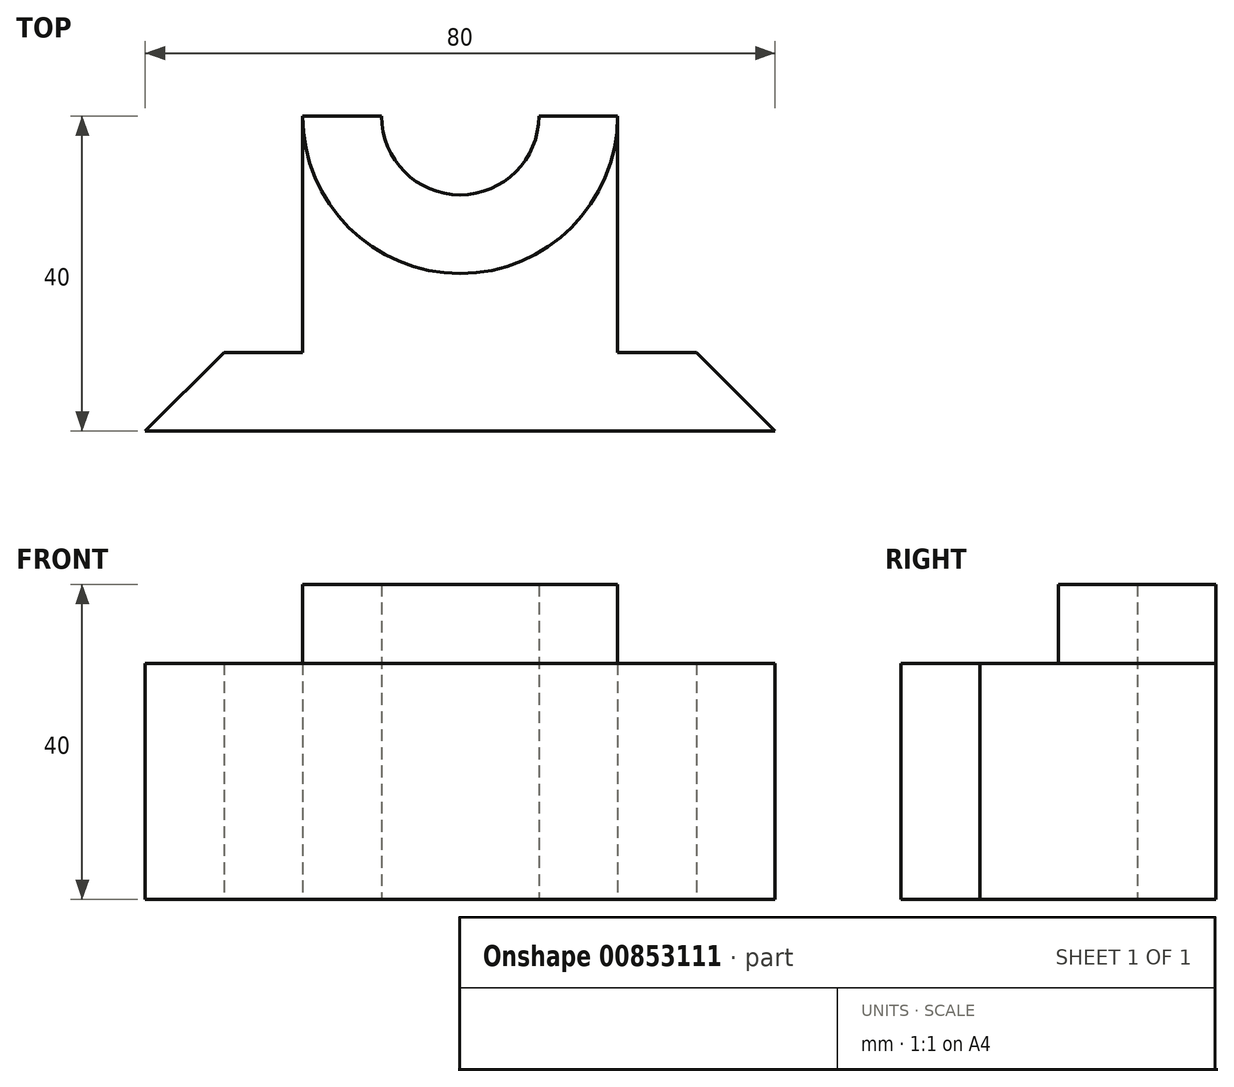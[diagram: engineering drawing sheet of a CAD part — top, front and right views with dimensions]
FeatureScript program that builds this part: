
annotation { "Feature Type Name" : "Feature", "Feature Type Description" : "" }
export const myFeature = defineFeature(function(context is Context, id is Id, definition is map)
    precondition{}
    {
        {
            var Q0;
            Q0=qCreatedBy(makeId("Top.planeOp"),FACE);
            var sketch = newSketch(context, id + "F0", { "sketchPlane" : qUnion([Q0])});
            skLineSegment(sketch, "E0", {"start": v(0, 30) * mm, "end": v(0, 0) * mm});
            skLineSegment(sketch, "E1", {"start": v(0, 0) * mm, "end": v(-40, 0) * mm});
            skLineSegment(sketch, "E2", {"start": v(-40, 0) * mm, "end": v(-30, 10) * mm});
            skLineSegment(sketch, "E3", {"start": v(-30, 10) * mm, "end": v(-20, 10) * mm});
            skLineSegment(sketch, "E4", {"start": v(-20, 10) * mm, "end": v(-20, 40) * mm});
            skLineSegment(sketch, "E5", {"start": v(-20, 40) * mm, "end": v(-10, 40) * mm});
            skArc(sketch, "E6", {"start": v(-20, 40) * mm, "mid": v(-14.14, 25.86) * mm, "end": v(0, 20) * mm});
            skArc(sketch, "E7", {"start": v(-10, 40) * mm, "mid": v(-7.07, 32.93) * mm, "end": v(0, 30) * mm});
            skLineSegment(sketch, "E8.MirrorCS", {"start": v(20, 10) * mm, "end": v(20, 40) * mm});
            skLineSegment(sketch, "E9.MirrorCS", {"start": v(30, 10) * mm, "end": v(20, 10) * mm});
            skLineSegment(sketch, "E10.MirrorCS", {"start": v(40, 0) * mm, "end": v(30, 10) * mm});
            skLineSegment(sketch, "E11.MirrorCS", {"start": v(0, 0) * mm, "end": v(40, 0) * mm});
            skLineSegment(sketch, "E12.MirrorCS", {"start": v(20, 40) * mm, "end": v(10, 40) * mm});
            skArc(sketch, "E13.MirrorCS", {"start": v(20, 40) * mm, "mid": v(14.14, 25.86) * mm, "end": v(0, 20) * mm});
            skArc(sketch, "E14.MirrorCS", {"start": v(10, 40) * mm, "mid": v(7.07, 32.93) * mm, "end": v(0, 30) * mm});
            skSolve(sketch);
        }
        {
            var Q0;
            Q0=makeQuery(id+"F0.imprint","IMPRINT",FACE,{"disambiguationData":[TD([[makeQuery(id+"F0.imprint","IMPRINT",EDGE,{"derivedFrom":sQuery(id+"F0.wireOp",EDGE,"E12.MirrorCS")}),1.0]])]});
            var Q1;
            Q1=makeQuery(id+"F0.imprint","IMPRINT",FACE,{"disambiguationData":[TD([[makeQuery(id+"F0.imprint","IMPRINT",EDGE,{"derivedFrom":sQuery(id+"F0.wireOp",EDGE,"E5")}),-1.0]])]});
            extrude(context, id + "F1", {"entities" : qUnion([Q0, Q1]), "depth" : 40 * mm, "offsetDistance" : 25 * mm});
        }
        {
            var Q0;
            {var subQ0=sQuery(id+"F0.wireOp",EDGE,"E1");Q0=makeQuery(id+"F0.imprint","IMPRINT",FACE,{"disambiguationData":[TD([[makeQuery(id+"F0.imprint","IMPRINT",EDGE,{"derivedFrom":subQ0}),-1.0]])]});}
            var Q1;
            Q1=makeQuery(id+"F0.imprint","IMPRINT",FACE,{"disambiguationData":[TD([[makeQuery(id+"F0.imprint","IMPRINT",EDGE,{"derivedFrom":sQuery(id+"F0.wireOp",EDGE,"E8.MirrorCS")}),1.0]])]});
            extrude(context, id + "F2", {"entities" : qUnion([Q0, Q1]), "operationType" : NewBodyOperationType.ADD, "depth" : 30 * mm, "offsetDistance" : 25 * mm});
        }
    });
